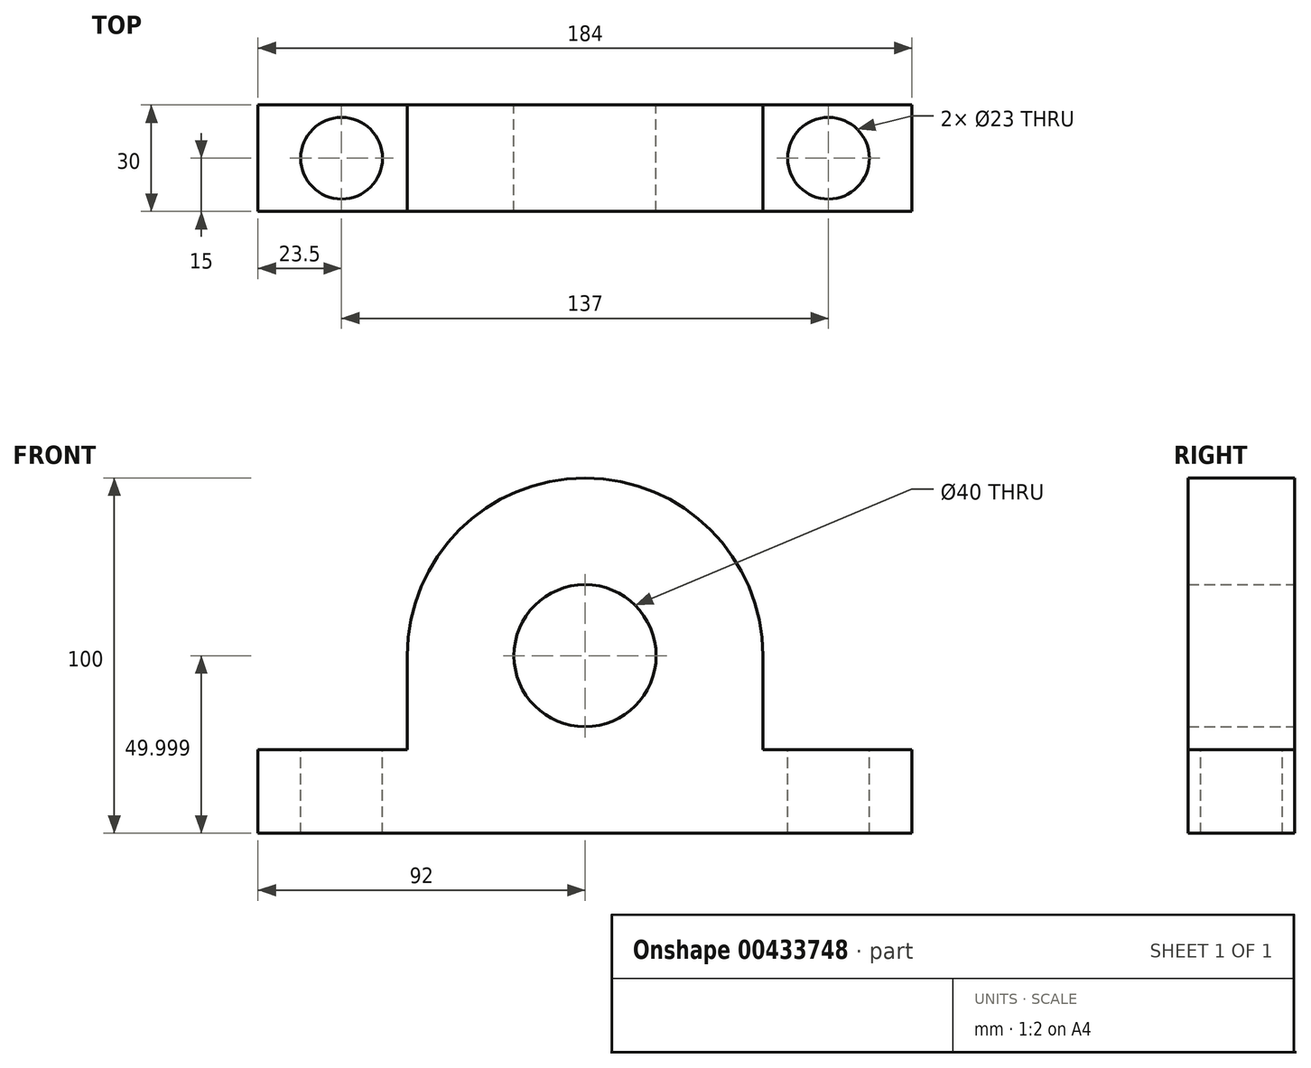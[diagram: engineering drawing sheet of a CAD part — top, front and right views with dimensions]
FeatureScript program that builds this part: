
annotation { "Feature Type Name" : "Feature", "Feature Type Description" : "" }
export const myFeature = defineFeature(function(context is Context, id is Id, definition is map)
    precondition{}
    {
        {
            var Q0;
            Q0=qCreatedBy(makeId("Front.planeOp"),FACE);
            var sketch = newSketch(context, id + "F0", { "sketchPlane" : qUnion([Q0])});
            skLineSegment(sketch, "E0.bottom", {"start": v(-92, -20.46) * mm, "end": v(92, -20.46) * mm});
            skLineSegment(sketch, "E0.top", {"start": v(-92, -43.95) * mm, "end": v(92, -43.95) * mm});
            skLineSegment(sketch, "E0.left", {"start": v(-92, -20.46) * mm, "end": v(-92, -43.95) * mm});
            skLineSegment(sketch, "E0.right", {"start": v(92, -20.46) * mm, "end": v(92, -43.95) * mm});
            skCircle(sketch, "E1", {"center": v(0, 6.05) * mm, "radius": 50 * mm});
            skCircle(sketch, "E2", {"center": v(0, 6.05) * mm, "radius": 20 * mm});
            skLineSegment(sketch, "E3", {"start": v(0, 6.05) * mm, "end": v(-50, 6.05) * mm});
            skLineSegment(sketch, "E4", {"start": v(-50, 6.05) * mm, "end": v(50, 6.05) * mm});
            skLineSegment(sketch, "E5", {"start": v(50, 6.05) * mm, "end": v(50, -20.46) * mm});
            skLineSegment(sketch, "E6", {"start": v(-50, 6.05) * mm, "end": v(-50, -20.46) * mm});
            skSolve(sketch);
        }
        {
            var Q0;
            Q0 = qSketchRegion(id + "F0", true);
            extrude(context, id + "F1", {"entities" : qUnion([Q0]), "depth" : 30 * mm, "offsetDistance" : 25 * mm});
        }
        {
            var Q0;
            {var subQ0=sQuery(id+"F0.wireOp",EDGE,"E0.bottom");Q0=makeQuery(id+"F1.opExtrude","SWEPT_FACE",FACE,{"disambiguationData":[OSD([subQ0]),TDD([makeQuery(id+"F0.imprint","IMPRINT",EDGE,{"disambiguationData":[TD([[makeQuery(id+"F0.imprint","INTERSECT",VERTEX,{"derivedFrom":[subQ0,sQuery(id+"F0.wireOp",EDGE,"E0.left")]}),-1.0]])],"derivedFrom":subQ0})])]});}
            var sketch = newSketch(context, id + "F2", { "sketchPlane" : qUnion([Q0])});
            skCircle(sketch, "E7", {"center": v(-68.5, -15) * mm, "radius": 11.5 * mm});
            skCircle(sketch, "E8", {"center": v(68.5, -15) * mm, "radius": 11.5 * mm});
            skSolve(sketch);
        }
        {
            var Q0;
            Q0=sQuery(id+"F2.wireOp",VERTEX,"E7.center");
            var Q1;
            Q1=sQuery(id+"F2.wireOp",VERTEX,"E8.center");
            var Q2;
            Q2=makeQuery(id+"F1.opExtrude","SWEPT_BODY",BODY,{"disambiguationData":[OSD([sQuery(id+"F0.wireOp",EDGE,"E0.bottom"),sQuery(id+"F0.wireOp",EDGE,"E0.top"),sQuery(id+"F0.wireOp",EDGE,"E0.left"),sQuery(id+"F0.wireOp",EDGE,"E0.right"),sQuery(id+"F0.wireOp",EDGE,"E1"),sQuery(id+"F0.wireOp",EDGE,"E2"),sQuery(id+"F0.wireOp",EDGE,"E5"),sQuery(id+"F0.wireOp",EDGE,"E6")])]});
            hole(context, id + "F3", {"style" : HoleStyle.SIMPLE, "endStyle" : HoleEndStyle.THROUGH, "holeDiameter" : 23 * mm, "majorDiameter" : 5 * mm, "isTappedThrough" : true, "tappedDepth" : 12 * mm, "tapClearance" : 3, "locations" : qUnion([Q0, Q1]), "scope" : qUnion([Q2])});
        }
    });
